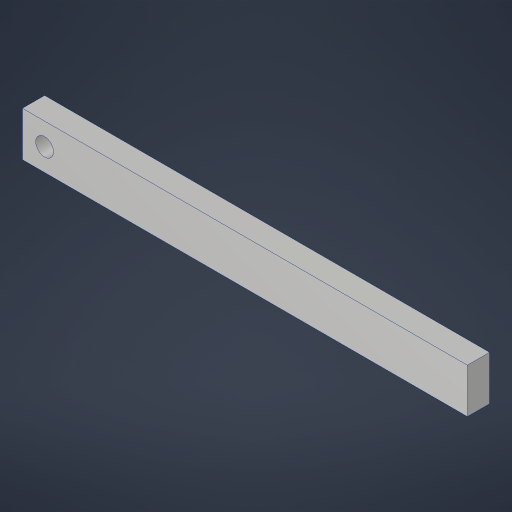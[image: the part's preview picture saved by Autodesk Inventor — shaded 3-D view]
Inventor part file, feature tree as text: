
AUTODESK INVENTOR PART (.ipt)
format: ipt  version: 2023.4 (Build 274418000, 418)  size: 164,352 bytes
history: native  units: in
note: dims shown in document units (in); Inventor stores cm internally (conversion verified against a paired STEP export)
features: sketch x1, extrude x1, hole x1
ambient origin geometry x8: Origin, YZ Plane, XZ Plane, XY Plane, X Axis, Y Axis, Z Axis, Center Point
bodies: Solid1 (feature_tree)
feature tree (3):
  sketch  "Sketch1"  dims[d0=5.0in d1=0.5in d2=0.25in d3=0.25in d4=0.0in d5=0.201in d6=0.75in d7=0.385in d8=0.25in d9=0.5635in d10=1.0in d11=0.8108in]
  extrude  "Extrusion1"  Depth=0.5in
  hole  "Hole1"  [1 undecoded]
note: 1 required parameter value undecoded (feature->parameter linkage not recoverable at this tier; creation-order binding heuristic only, values carry confidence <= 0.55)
